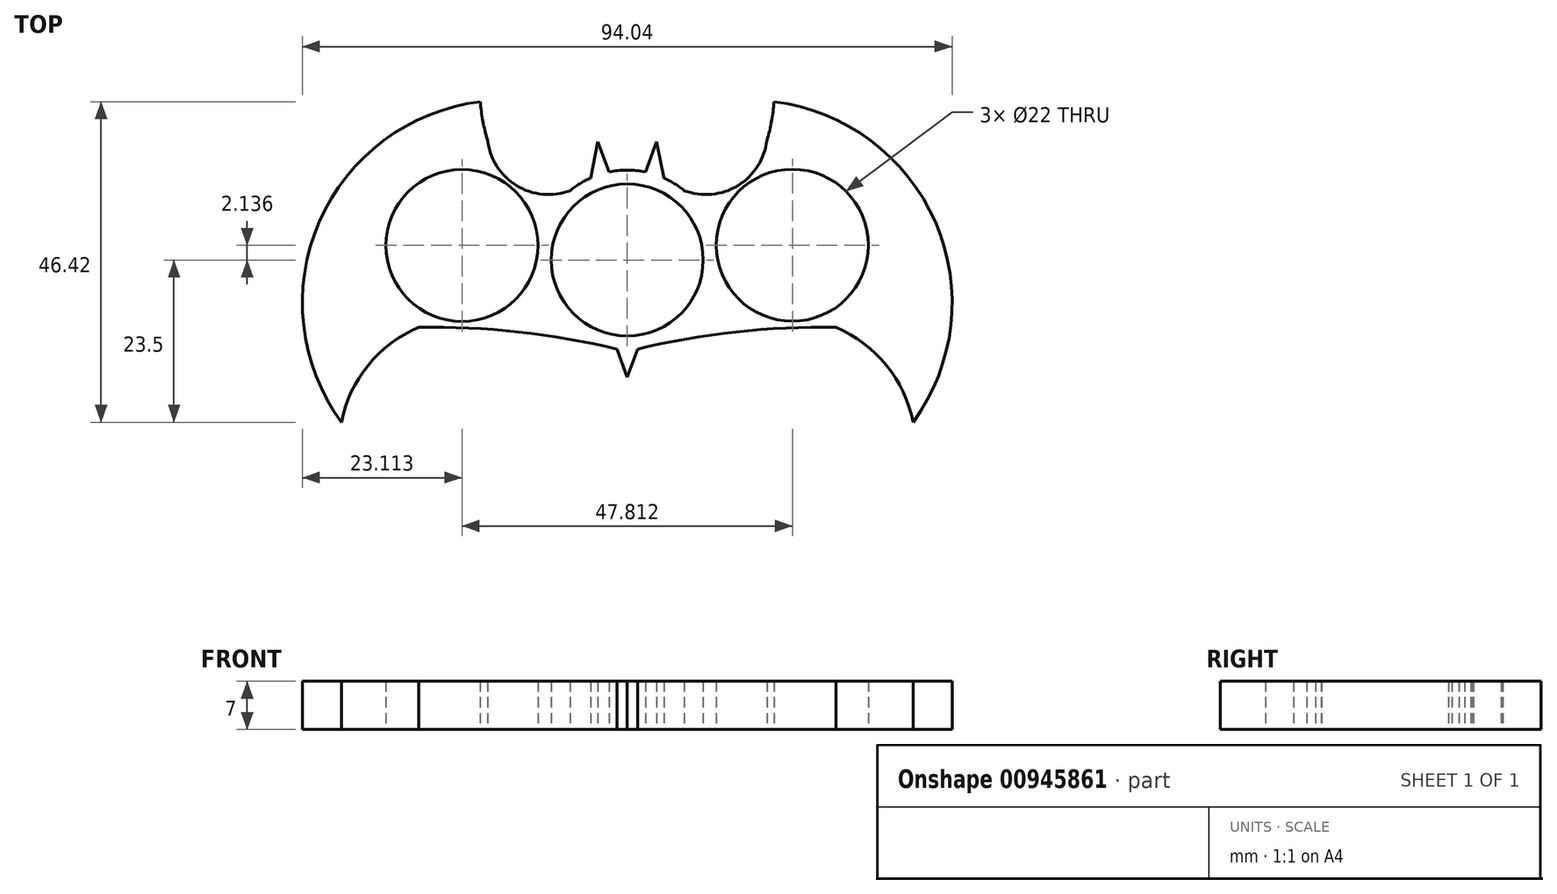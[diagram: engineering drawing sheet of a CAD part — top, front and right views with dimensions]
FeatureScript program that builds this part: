
annotation { "Feature Type Name" : "Feature", "Feature Type Description" : "" }
export const myFeature = defineFeature(function(context is Context, id is Id, definition is map)
    precondition{}
    {
        {
            var Q0;
            Q0=qCreatedBy(makeId("Top.planeOp"),FACE);
            var sketch = newSketch(context, id + "F0", { "sketchPlane" : qUnion([Q0])});
            skCircle(sketch, "E0", {"center": v(0, 0) * mm, "radius": 11 * mm});
            skCircle(sketch, "E1.0", {"center": v(0, 0) * mm, "radius": 13 * mm});
            skCircle(sketch, "E2", {"center": v(-23.9, 2.1) * mm, "radius": 11 * mm});
            skCircle(sketch, "E3", {"center": v(23.9, 2.14) * mm, "radius": 11 * mm});
            skLineSegment(sketch, "E4", {"start": v(-1.48, -12.92) * mm, "end": v(0, -16.95) * mm});
            skLineSegment(sketch, "E5", {"start": v(1.48, -12.92) * mm, "end": v(0, -16.95) * mm});
            skLineSegment(sketch, "E6", {"start": v(-5.3, 11.87) * mm, "end": v(-4.27, 17.13) * mm});
            skLineSegment(sketch, "E7", {"start": v(-4.27, 17.13) * mm, "end": v(-2.64, 12.73) * mm});
            skArc(sketch, "E8", {"start": v(-20.22, 17.35) * mm, "mid": v(-14.44, 10.02) * mm, "end": v(-5.3, 11.87) * mm});
            skLineSegment(sketch, "E9.MirrorCS", {"start": v(4.27, 17.13) * mm, "end": v(2.64, 12.73) * mm});
            skLineSegment(sketch, "E10.MirrorCS", {"start": v(5.3, 11.87) * mm, "end": v(4.27, 17.13) * mm});
            skArc(sketch, "E11.MirrorCS", {"start": v(20.22, 17.35) * mm, "mid": v(14.44, 10.02) * mm, "end": v(5.3, 11.87) * mm});
            skArc(sketch, "E12", {"start": v(-1.48, -12.92) * mm, "mid": v(-15.74, -10.43) * mm, "end": v(-30.2, -9.75) * mm});
            skArc(sketch, "E13.MirrorCS", {"start": v(1.48, -12.92) * mm, "mid": v(15.74, -10.43) * mm, "end": v(30.2, -9.75) * mm});
            skArc(sketch, "E14", {"start": v(-21.26, 22.92) * mm, "mid": v(-20.9, 20.1) * mm, "end": v(-20.22, 17.35) * mm});
            skArc(sketch, "E15.MirrorCS", {"start": v(21.26, 22.92) * mm, "mid": v(20.9, 20.1) * mm, "end": v(20.22, 17.35) * mm});
            skArc(sketch, "E16", {"start": v(-21.26, 22.92) * mm, "mid": v(-44.6, 5.47) * mm, "end": v(-41.37, -23.5) * mm});
            skArc(sketch, "E17", {"start": v(-30.2, -9.75) * mm, "mid": v(-37.5, -15.24) * mm, "end": v(-41.37, -23.5) * mm});
            skArc(sketch, "E18.MirrorCS", {"start": v(21.26, 22.92) * mm, "mid": v(44.6, 5.47) * mm, "end": v(41.37, -23.5) * mm});
            skArc(sketch, "E19.MirrorCS", {"start": v(30.2, -9.75) * mm, "mid": v(37.5, -15.24) * mm, "end": v(41.37, -23.5) * mm});
            skSolve(sketch);
        }
        {
            var Q0;
            {var subQ0=sQuery(id+"F0.wireOp",EDGE,"E11.MirrorCS");var subQ1=sQuery(id+"F0.wireOp",EDGE,"E1.0");var subQ3=makeQuery(id+"F0.imprint","INTERSECT",VERTEX,{"derivedFrom":[subQ1,subQ0]});Q0=makeQuery(id+"F0.imprint","IMPRINT",FACE,{"disambiguationData":[TD([[makeQuery(id+"F0.imprint","IMPRINT",EDGE,{"disambiguationData":[TD([[subQ3,-1.0]])],"derivedFrom":subQ1}),1.0]])]});}
            var Q1;
            {var subQ0=sQuery(id+"F0.wireOp",EDGE,"E9.MirrorCS");Q1=makeQuery(id+"F0.imprint","IMPRINT",FACE,{"disambiguationData":[TD([[makeQuery(id+"F0.imprint","IMPRINT",EDGE,{"derivedFrom":subQ0}),1.0]])]});}
            var Q2;
            {var subQ0=sQuery(id+"F0.wireOp",EDGE,"E6");Q2=makeQuery(id+"F0.imprint","IMPRINT",FACE,{"disambiguationData":[TD([[makeQuery(id+"F0.imprint","IMPRINT",EDGE,{"derivedFrom":subQ0}),-1.0]])]});}
            var Q3;
            {var subQ0=sQuery(id+"F0.wireOp",EDGE,"E8");var subQ1=sQuery(id+"F0.wireOp",EDGE,"E1.0");var subQ3=makeQuery(id+"F0.imprint","INTERSECT",VERTEX,{"derivedFrom":[subQ1,subQ0]});Q3=makeQuery(id+"F0.imprint","IMPRINT",FACE,{"disambiguationData":[TD([[makeQuery(id+"F0.imprint","IMPRINT",EDGE,{"disambiguationData":[TD([[subQ3,1.0]])],"derivedFrom":subQ1}),1.0]])]});}
            var Q4;
            {var subQ0=sQuery(id+"F0.wireOp",EDGE,"vy9nJhJj-oGlm-wzQs-hRE9-by593pWwjnNt");var subQ1=sQuery(id+"F0.wireOp",EDGE,"E1.0");var subQ3=makeQuery(id+"F0.imprint","INTERSECT",VERTEX,{"derivedFrom":[subQ1,subQ0]});Q4=makeQuery(id+"F0.imprint","IMPRINT",FACE,{"disambiguationData":[TD([[makeQuery(id+"F0.imprint","IMPRINT",EDGE,{"disambiguationData":[TD([[subQ3,-1.0]])],"derivedFrom":subQ1}),1.0]])]});}
            var Q5;
            {var subQ0=sQuery(id+"F0.wireOp",EDGE,"E4");Q5=makeQuery(id+"F0.imprint","IMPRINT",FACE,{"disambiguationData":[TD([[makeQuery(id+"F0.imprint","IMPRINT",EDGE,{"derivedFrom":subQ0}),1.0]])]});}
            var Q6;
            {var subQ0=sQuery(id+"F0.wireOp",EDGE,"de59702b-cbcf-4cb2-8226-e8e6dd1689ab0.MirrorCS");var subQ1=sQuery(id+"F0.wireOp",EDGE,"E1.0");var subQ3=makeQuery(id+"F0.imprint","INTERSECT",VERTEX,{"derivedFrom":[subQ1,subQ0]});Q6=makeQuery(id+"F0.imprint","IMPRINT",FACE,{"disambiguationData":[TD([[makeQuery(id+"F0.imprint","IMPRINT",EDGE,{"disambiguationData":[TD([[subQ3,1.0]])],"derivedFrom":subQ1}),1.0]])]});}
            var Q7;
            {var subQ0=sQuery(id+"F0.wireOp",EDGE,"a0217071-82d7-42f5-8362-938ac820c6e80.MirrorCS");Q7=makeQuery(id+"F0.imprint","IMPRINT",FACE,{"disambiguationData":[TD([[makeQuery(id+"F0.imprint","IMPRINT",EDGE,{"derivedFrom":subQ0}),1.0]])]});}
            var Q8;
            {var subQ0=sQuery(id+"F0.wireOp",EDGE,"jAyZC5Du-sEvD-Z4HX-caJO-tt9of81L5LYD");Q8=makeQuery(id+"F0.imprint","IMPRINT",FACE,{"disambiguationData":[TD([[makeQuery(id+"F0.imprint","IMPRINT",EDGE,{"derivedFrom":subQ0}),-1.0]])]});}
            var Q9;
            {var subQ0=sQuery(id+"F0.wireOp",EDGE,"vy9nJhJj-oGlm-wzQs-hRE9-by593pWwjnNt");var subQ1=sQuery(id+"F0.wireOp",EDGE,"E1.0");var subQ2=makeQuery(id+"F0.imprint","INTERSECT",VERTEX,{"derivedFrom":[subQ1,subQ0]});Q9=makeQuery(id+"F0.imprint","IMPRINT",FACE,{"disambiguationData":[TD([[makeQuery(id+"F0.imprint","IMPRINT",EDGE,{"disambiguationData":[TD([[subQ2,1.0]])],"derivedFrom":subQ1}),-1.0]])]});}
            var Q10;
            {var subQ0=sQuery(id+"F0.wireOp",EDGE,"de59702b-cbcf-4cb2-8226-e8e6dd1689ab0.MirrorCS");var subQ1=sQuery(id+"F0.wireOp",EDGE,"E1.0");var subQ2=makeQuery(id+"F0.imprint","INTERSECT",VERTEX,{"derivedFrom":[subQ1,subQ0]});Q10=makeQuery(id+"F0.imprint","IMPRINT",FACE,{"disambiguationData":[TD([[makeQuery(id+"F0.imprint","IMPRINT",EDGE,{"disambiguationData":[TD([[subQ2,-1.0]])],"derivedFrom":subQ1}),-1.0]])]});}
            var Q11;
            Q11=makeQuery(id+"F0.imprint","IMPRINT",FACE,{"disambiguationData":[TD([[makeQuery(id+"F0.imprint","IMPRINT",EDGE,{"derivedFrom":sQuery(id+"F0.wireOp",EDGE,"E0")}),-1.0]])]});
            extrude(context, id + "F1", {"entities" : qUnion([Q0, Q1, Q2, Q3, Q4, Q5, Q6, Q7, Q8, Q9, Q10, Q11]), "depth" : 7 * mm, "offsetDistance" : 25 * mm});
        }
    });
